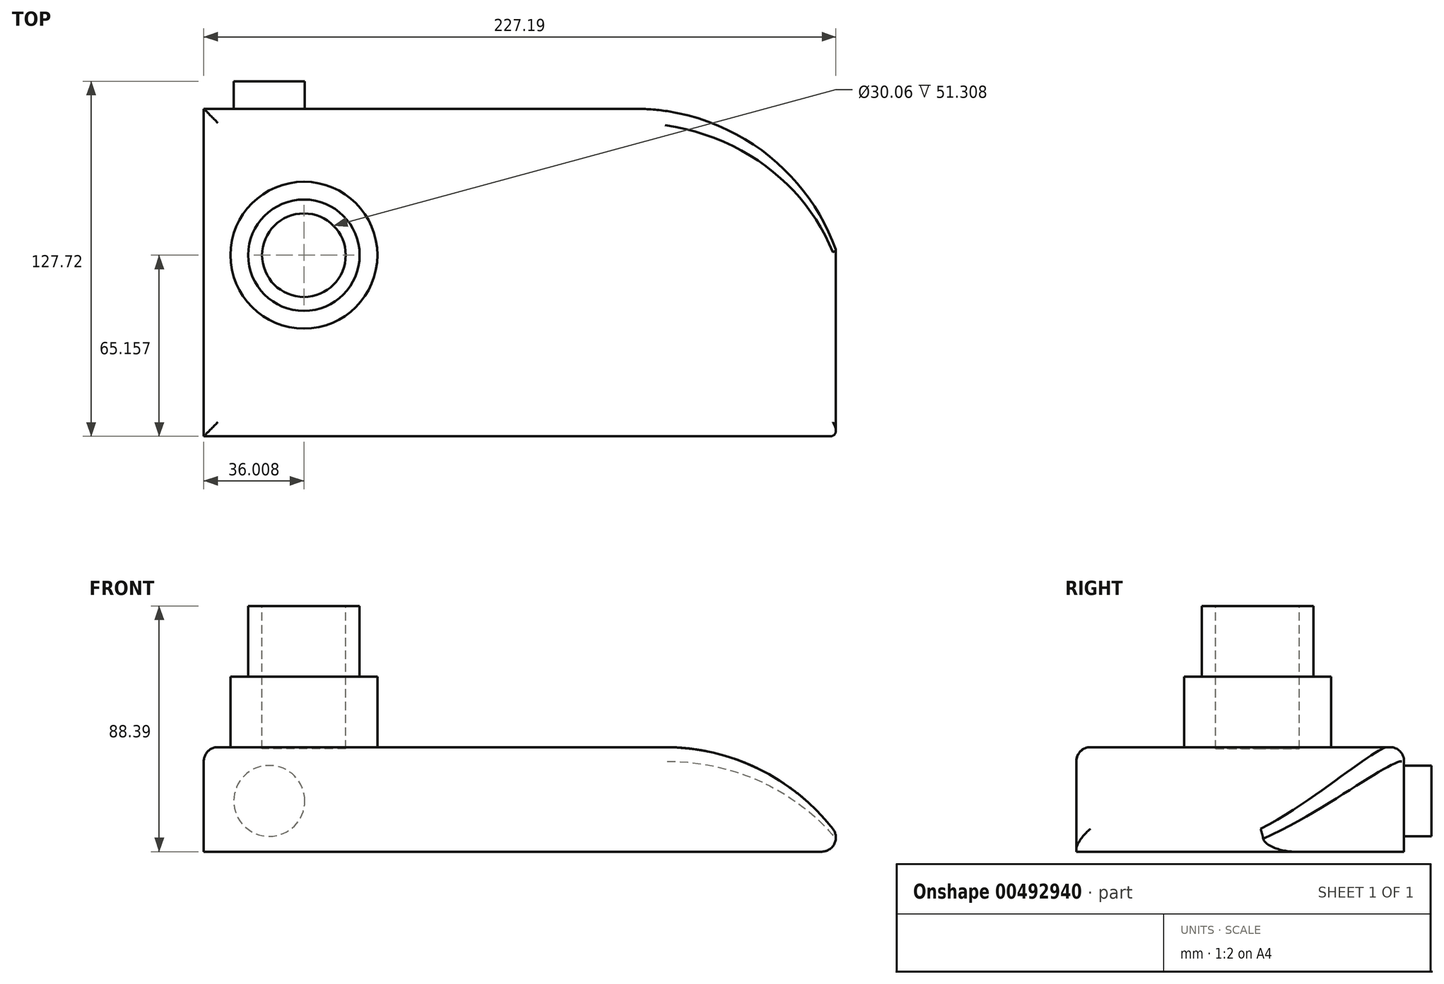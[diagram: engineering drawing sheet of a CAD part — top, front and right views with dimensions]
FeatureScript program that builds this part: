
annotation { "Feature Type Name" : "Feature", "Feature Type Description" : "" }
export const myFeature = defineFeature(function(context is Context, id is Id, definition is map)
    precondition{}
    {
        {
            var Q0;
            Q0=qCreatedBy(makeId("Top.planeOp"),FACE);
            var sketch = newSketch(context, id + "F0", { "sketchPlane" : qUnion([Q0])});
            skLineSegment(sketch, "E0.bottom", {"start": v(-147.16, 57.1) * mm, "end": v(84.56, 57.1) * mm});
            skLineSegment(sketch, "E0.top", {"start": v(-147.16, -60.7) * mm, "end": v(84.56, -60.7) * mm});
            skLineSegment(sketch, "E0.left", {"start": v(-147.16, 57.1) * mm, "end": v(-147.16, -60.7) * mm});
            skLineSegment(sketch, "E0.right", {"start": v(84.56, 57.1) * mm, "end": v(84.56, -60.7) * mm});
            skSolve(sketch);
        }
        {
            var Q0;
            Q0 = qSketchRegion(id + "F0", true);
            extrude(context, id + "F1", {"entities" : qUnion([Q0]), "depth" : 19.3 * mm});
        }
        {
            var Q0;
            Q0=makeQuery(id+"F1.opExtrude","CAP_FACE",FACE,{"disambiguationData":[OSD([sQuery(id+"F0.wireOp",EDGE,"E0.bottom"),sQuery(id+"F0.wireOp",EDGE,"E0.top"),sQuery(id+"F0.wireOp",EDGE,"E0.left"),sQuery(id+"F0.wireOp",EDGE,"E0.right")])],"isStart":false});
            extrude(context, id + "F2", {"entities" : qUnion([Q0]), "operationType" : NewBodyOperationType.ADD, "depth" : 18.29 * mm});
        }
        {
            var Q0;
            Q0=makeQuery(id+"F2.opExtrude","CAP_EDGE",EDGE,{"disambiguationData":[OSD([sQuery(id+"F0.wireOp",EDGE,"E0.right")])],"isStart":false});
            var Q1;
            {var subQ0=sQuery(id+"F0.wireOp",EDGE,"E0.right");var subQ1=sQuery(id+"F0.wireOp",EDGE,"E0.bottom");Q1=makeQuery(id+"F2.boolean.opBoolean","MERGE",EDGE,{"derivedFrom":[makeQuery(id+"F1.opExtrude","SWEPT_EDGE",EDGE,{"disambiguationData":[OSD([subQ1,subQ0])]}),makeQuery(id+"F2.opExtrude","SWEPT_EDGE",EDGE,{"disambiguationData":[OSD([subQ1,subQ0])]})]});}
            fillet(context, id + "F3", {"entities" : qUnion([Q0, Q1]), "radius" : 76.65 * mm, "tangentPropagation" : true, "allowEdgeOverflow" : false});
        }
        {
            var Q0;
            Q0=makeQuery(id+"F2.opExtrude","CAP_FACE",FACE,{"disambiguationData":[OSD([sQuery(id+"F0.wireOp",EDGE,"E0.bottom"),sQuery(id+"F0.wireOp",EDGE,"E0.top"),sQuery(id+"F0.wireOp",EDGE,"E0.left"),sQuery(id+"F0.wireOp",EDGE,"E0.right")])],"isStart":false});
            fillet(context, id + "F4", {"entities" : qUnion([Q0]), "radius" : 5.08 * mm, "tangentPropagation" : true, "allowEdgeOverflow" : false});
        }
        {
            var Q0;
            Q0=makeQuery(id+"F2.opExtrude","CAP_FACE",FACE,{"disambiguationData":[OSD([sQuery(id+"F0.wireOp",EDGE,"E0.bottom"),sQuery(id+"F0.wireOp",EDGE,"E0.top"),sQuery(id+"F0.wireOp",EDGE,"E0.left"),sQuery(id+"F0.wireOp",EDGE,"E0.right")])],"isStart":false});
            var sketch = newSketch(context, id + "F5", { "sketchPlane" : qUnion([Q0])});
            skCircle(sketch, "E1", {"center": v(-111.15, 4.45) * mm, "radius": 26.4 * mm});
            skSolve(sketch);
        }
        {
            var Q0;
            Q0 = qSketchRegion(id + "F5", true);
            extrude(context, id + "F6", {"entities" : qUnion([Q0]), "operationType" : NewBodyOperationType.ADD, "depth" : 25.4 * mm});
        }
        {
            var Q0;
            Q0=makeQuery(id+"F6.opExtrude","CAP_FACE",FACE,{"disambiguationData":[OSD([sQuery(id+"F5.wireOp",EDGE,"E1")])],"isStart":false});
            var sketch = newSketch(context, id + "F7", { "sketchPlane" : qUnion([Q0])});
            skCircle(sketch, "E2", {"center": v(-111.15, 4.45) * mm, "radius": 20.03 * mm});
            skSolve(sketch);
        }
        {
            var Q0;
            Q0 = qSketchRegion(id + "F7", true);
            extrude(context, id + "F8", {"entities" : qUnion([Q0]), "operationType" : NewBodyOperationType.ADD, "depth" : 25.4 * mm});
        }
        {
            var Q0;
            Q0=makeQuery(id+"F8.opExtrude","CAP_FACE",FACE,{"disambiguationData":[OSD([sQuery(id+"F7.wireOp",EDGE,"E2")])],"isStart":false});
            var sketch = newSketch(context, id + "F9", { "sketchPlane" : qUnion([Q0])});
            skCircle(sketch, "E3", {"center": v(-111.15, 4.45) * mm, "radius": 15.03 * mm});
            skSolve(sketch);
        }
        {
            var Q0;
            Q0 = qSketchRegion(id + "F9", true);
            extrude(context, id + "F10", {"entities" : qUnion([Q0]), "operationType" : NewBodyOperationType.REMOVE, "oppositeDirection" : true, "depth" : 51.3 * mm});
        }
        {
            var Q0;
            {var subQ0=sQuery(id+"F0.wireOp",EDGE,"E0.bottom");Q0=makeQuery(id+"F2.boolean.opBoolean","MERGE",FACE,{"derivedFrom":[makeQuery(id+"F1.opExtrude","SWEPT_FACE",FACE,{"disambiguationData":[OSD([subQ0])]}),makeQuery(id+"F2.opExtrude","SWEPT_FACE",FACE,{"disambiguationData":[OSD([subQ0])]})]});}
            var sketch = newSketch(context, id + "F11", { "sketchPlane" : qUnion([Q0])});
            skCircle(sketch, "E4", {"center": v(123.6, 18.25) * mm, "radius": 12.75 * mm});
            skSolve(sketch);
        }
        {
            var Q0;
            Q0=makeQuery(id+"F11.imprint","IMPRINT",FACE,{"disambiguationData":[TD([[makeQuery(id+"F11.imprint","IMPRINT",EDGE,{"derivedFrom":sQuery(id+"F11.wireOp",EDGE,"E4")}),1.0]])]});
            extrude(context, id + "F12", {"entities" : qUnion([Q0]), "operationType" : NewBodyOperationType.ADD, "depth" : 9.9 * mm});
        }
    });
